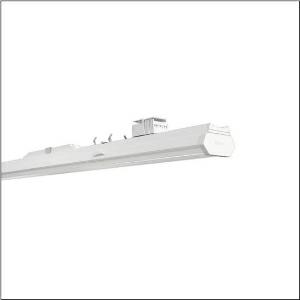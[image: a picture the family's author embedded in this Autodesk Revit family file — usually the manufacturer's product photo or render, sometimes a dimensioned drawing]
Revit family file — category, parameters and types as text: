
# Revit family: licross_r__21_performance_mo_52td167n46xg_c3aa
name_source: partatom
category: Lighting Fixtures
units: mm (PartAtom-declared; Revit-internal decimal feet)

## family parameters
Cut with Voids When Loaded = No
Host = Face
Light Source = No
Part Type = Normal
Room Calculation Point = No
Round Connector Dimension = Use Diameter
Shared = No

## types (1)
- Licross® 21 Performance MO (1 x LED, 6000 lm, 32.4 W, 4000K)
    Apparent Load = 32 VA
    CIE Flux Codes = 66 88 96 79 100
    Color Rendering = 80
    Color Temperature = 4000K
    Default Elevation = 1800 mm
    Description = Licross® 21 Performance MO, luminaire insert, of sheet steel, galvanised, coil coated, white, length: 1.500mm, width: 120mm, height: 123mm, LED rated luminous flux: 6.000lm, light colour: 840, control gear: ON/OFF, control gear: ECG, with plug, 3-pole, with phase selection, mains connection: 220..240V, AC, 50/60Hz, halogen-free wiring, primary light control with lens, of plastic, primary optical cover: cover, of PMMA, light emission: direct/indirect distribution, primary light characteristic: symmetric, protection rating (complete): IP54, insulation class (complete): insulation class I (protective earthing), certification: CE, ENEC, UKCA, protection symbol: D if used in an environment with non-conductive dust loads with corresponding accessories, impact resistance: IK06, permissible ambient temperature for indoor applications: -35..+50°C, corresponds to IFS (International Featured Standards) requirements for safety and quality in the food industry, reducing of maximum allowable ambient temperature of 5°C with ceiling mounting, LABS conformity tested according to VDMA 24364:2018-05, packaging unit: 1 piece
    Height = 114 mm
    Lamp = 1 x LED
    Lamp Light Flux = 6000 lm
    Lamp Power = 32.4 W
    Lamp count = 1
    Length = 1500 mm
    Luminous efficacy = 185 lm/W
    Manufacturer = Siteco
    ModVariant = No
    Model = 52TD167N46XG
    Mounting Place = Ceiling
    Mounting Type = Pendant
    Number of Poles = 1
    OnlyDefault = Yes
    Power Factor = 1
    Product Name = Licross® 21 Performance MO
    Product group = luminaire insert
    ProductGroupID = 902
    Protection Class = Protection class I
    Protection Degree = IP 54
    RLX_Detail_Level = 1
    RlxData = <blob elided: 28313 chars, md5=530da1e7>
    Socket = socket
    Standby Power = 0 W
    System Light Flux = 6000 lm
    System Power = 32 W
    Type Comments = Product without accessories
    Type Image = l_1256148.jpg
    URL = http://relux.com
    VarID = ---
    Voltage = 0 V
    Weight = 0.00 kg
    Width = 120 mm

## geometry (parser evidence)
native form markers: Blend x4, Sweep x10
no freeform markers — native parametric forms only
